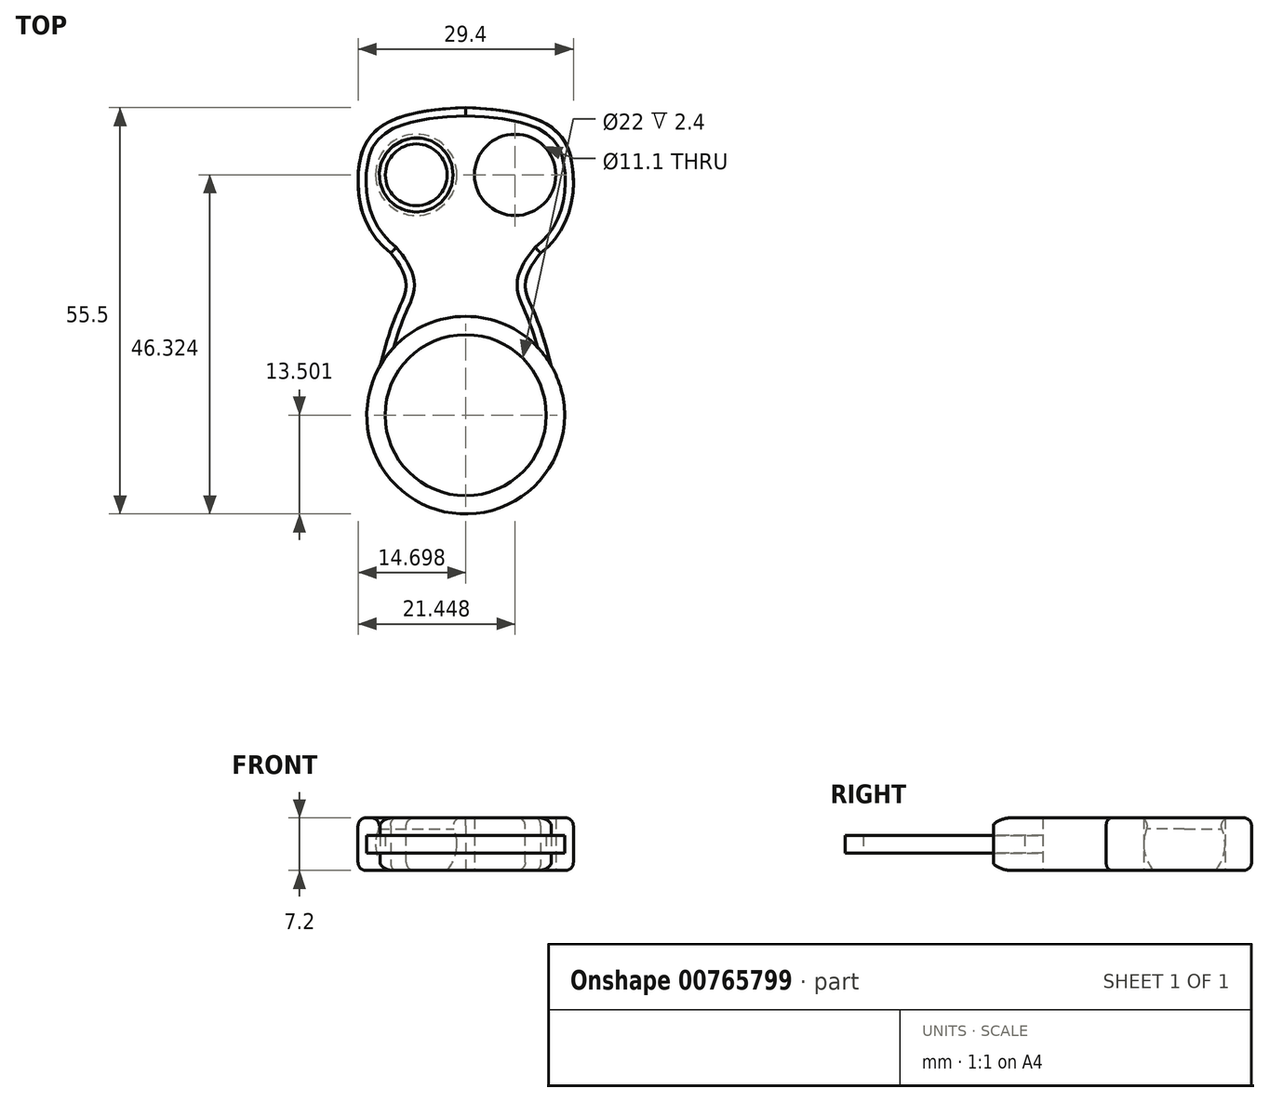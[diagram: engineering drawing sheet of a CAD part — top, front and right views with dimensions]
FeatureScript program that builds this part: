
annotation { "Feature Type Name" : "Feature", "Feature Type Description" : "" }
export const myFeature = defineFeature(function(context is Context, id is Id, definition is map)
    precondition{}
    {
        {
            var Q0;
            Q0=qCreatedBy(makeId("Top.planeOp"),FACE);
            var sketch = newSketch(context, id + "F0", { "sketchPlane" : qUnion([Q0])});
            skCircle(sketch, "E0", {"center": v(0, 0) * mm, "radius": 11 * mm});
            skCircle(sketch, "E1", {"center": v(0, 0) * mm, "radius": 13.5 * mm});
            skLineSegment(sketch, "E2", {"start": v(-60.62, 35) * mm, "end": v(57.4, -33.14) * mm, "construction": true});
            skLineSegment(sketch, "E3.MirrorCS", {"start": v(-60.62, -35) * mm, "end": v(57.4, 33.14) * mm, "construction": true});
            skFitSpline(sketch, "E4", {"points": [v(-11.7, 6.75) * mm, v(-8.5, 16) * mm, v(-10.25, 22.14) * mm], "startDerivative": vector(9.34, 35.35) * mm, "endDerivative": vector(-17.9, 20.96) * mm});
            skLineSegment(sketch, "E5", {"start": v(-61.07, 42) * mm, "end": v(58.93, 42) * mm, "construction": true});
            skFitSpline(sketch, "E6", {"points": [v(-10.25, 22.14) * mm, v(-14.64, 33.32) * mm, v(0, 42) * mm], "startDerivative": vector(-26.2, 21.36) * mm, "endDerivative": vector(68.91, 1.84) * mm});
            skCircle(sketch, "E7", {"center": v(-6.75, 32.82) * mm, "radius": 5.55 * mm});
            skFitSpline(sketch, "E8.MirrorCS", {"points": [v(10.25, 22.14) * mm, v(14.63, 33.32) * mm, v(0, 42) * mm], "startDerivative": vector(26.2, 21.36) * mm, "endDerivative": vector(-68.91, 1.84) * mm});
            skFitSpline(sketch, "E9.MirrorCS", {"points": [v(11.69, 6.75) * mm, v(8.5, 16) * mm, v(10.25, 22.14) * mm], "startDerivative": vector(-9.34, 35.35) * mm, "endDerivative": vector(17.9, 20.96) * mm});
            skCircle(sketch, "E10.MirrorC", {"center": v(6.75, 32.82) * mm, "radius": 5.55 * mm});
            skSolve(sketch);
        }
        {
            var Q0;
            Q0=qCreatedBy(makeId("Top.planeOp"),FACE);
            cPlane(context, id + "F1", {"entities" : qUnion([Q0]), "cplaneType" : CPlaneType.OFFSET, "offset" : 2.4 * mm, "width" : 150 * mm, "height" : 150 * mm});
        }
        {
            var Q0;
            Q0=qCreatedBy(id+"F1.planeOp",FACE);
            var sketch = newSketch(context, id + "F2", { "sketchPlane" : qUnion([Q0])});
            skCircle(sketch, "E11.0", {"center": v(0, 0) * mm, "radius": 13.5 * mm});
            skCircle(sketch, "E11.1", {"center": v(0, 0) * mm, "radius": 11 * mm});
            skSolve(sketch);
        }
        {
            var Q0;
            {var subQ0=sQuery(id+"F0.wireOp",EDGE,"E4");Q0=makeQuery(id+"F0.imprint","IMPRINT",FACE,{"disambiguationData":[TD([[makeQuery(id+"F0.imprint","IMPRINT",EDGE,{"derivedFrom":subQ0}),-1.0]])]});}
            var Q1;
            Q1=makeQuery(id+"F0.imprint","IMPRINT",FACE,{"disambiguationData":[TD([[makeQuery(id+"F0.imprint","IMPRINT",EDGE,{"derivedFrom":sQuery(id+"F0.wireOp",EDGE,"E7")}),1.0]])]});
            var Q2;
            Q2=makeQuery(id+"F0.imprint","IMPRINT",FACE,{"disambiguationData":[TD([[makeQuery(id+"F0.imprint","IMPRINT",EDGE,{"derivedFrom":sQuery(id+"F0.wireOp",EDGE,"E10.MirrorC")}),-1.0]])]});
            extrude(context, id + "F3", {"entities" : qUnion([Q0, Q1, Q2]), "depth" : 7.2 * mm, "offsetDistance" : 25 * mm});
        }
        {
            var Q0;
            Q0=qCreatedBy(makeId("Top.planeOp"),FACE);
            cPlane(context, id + "F4", {"entities" : qUnion([Q0]), "cplaneType" : CPlaneType.OFFSET, "offset" : 3.6 * mm, "width" : 150 * mm, "height" : 150 * mm});
        }
        {
            var Q0;
            Q0=qCreatedBy(id+"F4.planeOp",FACE);
            var sketch = newSketch(context, id + "F5", { "sketchPlane" : qUnion([Q0])});
            skArc(sketch, "E12.0", {"start": v(-1.2, 32.82) * mm, "mid": v(-6.75, 38.37) * mm, "end": v(-12.3, 32.82) * mm});
            skLineSegment(sketch, "E13", {"start": v(-12.3, 32.82) * mm, "end": v(-1.2, 32.82) * mm});
            skArc(sketch, "E14.0", {"start": v(1.2, 32.82) * mm, "mid": v(6.75, 38.37) * mm, "end": v(12.3, 32.82) * mm});
            skLineSegment(sketch, "E15", {"start": v(1.2, 32.82) * mm, "end": v(12.3, 32.82) * mm});
            skSolve(sketch);
        }
        {
            var Q0;
            Q0 = qSketchRegion(id + "F5", true);
            var Q1;
            Q1=sQuery(id+"F5.wireOp",EDGE,"E13");
            revolve(context, id + "F6", {"operationType" : NewBodyOperationType.REMOVE, "surfaceOperationType" : NewSurfaceOperationType.NEW, "entities" : qUnion([Q0]), "axis" : qUnion([Q1]), "revolveType" : RevolveType.FULL, "oppositeDirection" : true});
        }
        {
            var Q0;
            Q0=makeQuery(id+"F6.boolean.opBoolean","INTERSECT",EDGE,{"derivedFrom":[makeQuery(id+"F3.opExtrude","CAP_FACE",FACE,{"disambiguationData":[OSD([sQuery(id+"F0.wireOp",EDGE,"E1"),sQuery(id+"F0.wireOp",EDGE,"E4"),sQuery(id+"F0.wireOp",EDGE,"E6"),sQuery(id+"F0.wireOp",EDGE,"E8.MirrorCS"),sQuery(id+"F0.wireOp",EDGE,"E9.MirrorCS")])],"isStart":false}),makeQuery(id+"F6.opRevolve","SWEPT_FACE",FACE,{"disambiguationData":[OSD([sQuery(id+"F5.wireOp",EDGE,"E12.0")])]})]});
            var Q1;
            Q1=makeQuery(id+"F6.boolean.opBoolean","INTERSECT",EDGE,{"derivedFrom":[makeQuery(id+"F3.opExtrude","CAP_FACE",FACE,{"disambiguationData":[OSD([sQuery(id+"F0.wireOp",EDGE,"E1"),sQuery(id+"F0.wireOp",EDGE,"E4"),sQuery(id+"F0.wireOp",EDGE,"E6"),sQuery(id+"F0.wireOp",EDGE,"E8.MirrorCS"),sQuery(id+"F0.wireOp",EDGE,"E9.MirrorCS")])],"isStart":false}),makeQuery(id+"F6.opRevolve","SWEPT_FACE",FACE,{"disambiguationData":[OSD([sQuery(id+"F5.wireOp",EDGE,"E14.0")])]})]});
            fillet(context, id + "F7", {"entities" : qUnion([Q0, Q1]), "radius" : 1.1 * mm, "tangentPropagation" : true, "allowEdgeOverflow" : false});
        }
        {
            var Q0;
            Q0 = qSketchRegion(id + "F2", true);
            extrude(context, id + "F8", {"entities" : qUnion([Q0]), "depth" : 2.4 * mm, "offsetDistance" : 25 * mm});
        }
        {
            var Q0;
            Q0=makeQuery(id+"F3.opExtrude","CAP_EDGE",EDGE,{"disambiguationData":[OSD([sQuery(id+"F0.wireOp",EDGE,"E4")])],"isStart":false});
            var Q1;
            Q1=makeQuery(id+"F3.opExtrude","CAP_EDGE",EDGE,{"disambiguationData":[OSD([sQuery(id+"F0.wireOp",EDGE,"E4")])],"isStart":true});
            var Q2;
            Q2=makeQuery(id+"F3.opExtrude","CAP_EDGE",EDGE,{"disambiguationData":[OSD([sQuery(id+"F0.wireOp",EDGE,"E9.MirrorCS")])],"isStart":true});
            var Q3;
            Q3=makeQuery(id+"F3.opExtrude","CAP_EDGE",EDGE,{"disambiguationData":[OSD([sQuery(id+"F0.wireOp",EDGE,"E9.MirrorCS")])],"isStart":false});
            var Q4;
            Q4=makeQuery(id+"F3.opExtrude","CAP_EDGE",EDGE,{"disambiguationData":[OSD([sQuery(id+"F0.wireOp",EDGE,"E8.MirrorCS")])],"isStart":false});
            var Q5;
            Q5=makeQuery(id+"F3.opExtrude","CAP_EDGE",EDGE,{"disambiguationData":[OSD([sQuery(id+"F0.wireOp",EDGE,"E6")])],"isStart":false});
            var Q6;
            Q6=makeQuery(id+"F3.opExtrude","CAP_EDGE",EDGE,{"disambiguationData":[OSD([sQuery(id+"F0.wireOp",EDGE,"E6")])],"isStart":true});
            var Q7;
            Q7=makeQuery(id+"F3.opExtrude","CAP_EDGE",EDGE,{"disambiguationData":[OSD([sQuery(id+"F0.wireOp",EDGE,"E8.MirrorCS")])],"isStart":true});
            fillet(context, id + "F9", {"entities" : qUnion([Q0, Q1, Q2, Q3, Q4, Q5, Q6, Q7]), "radius" : 1.1 * mm, "tangentPropagation" : true, "allowEdgeOverflow" : false});
        }
    });
